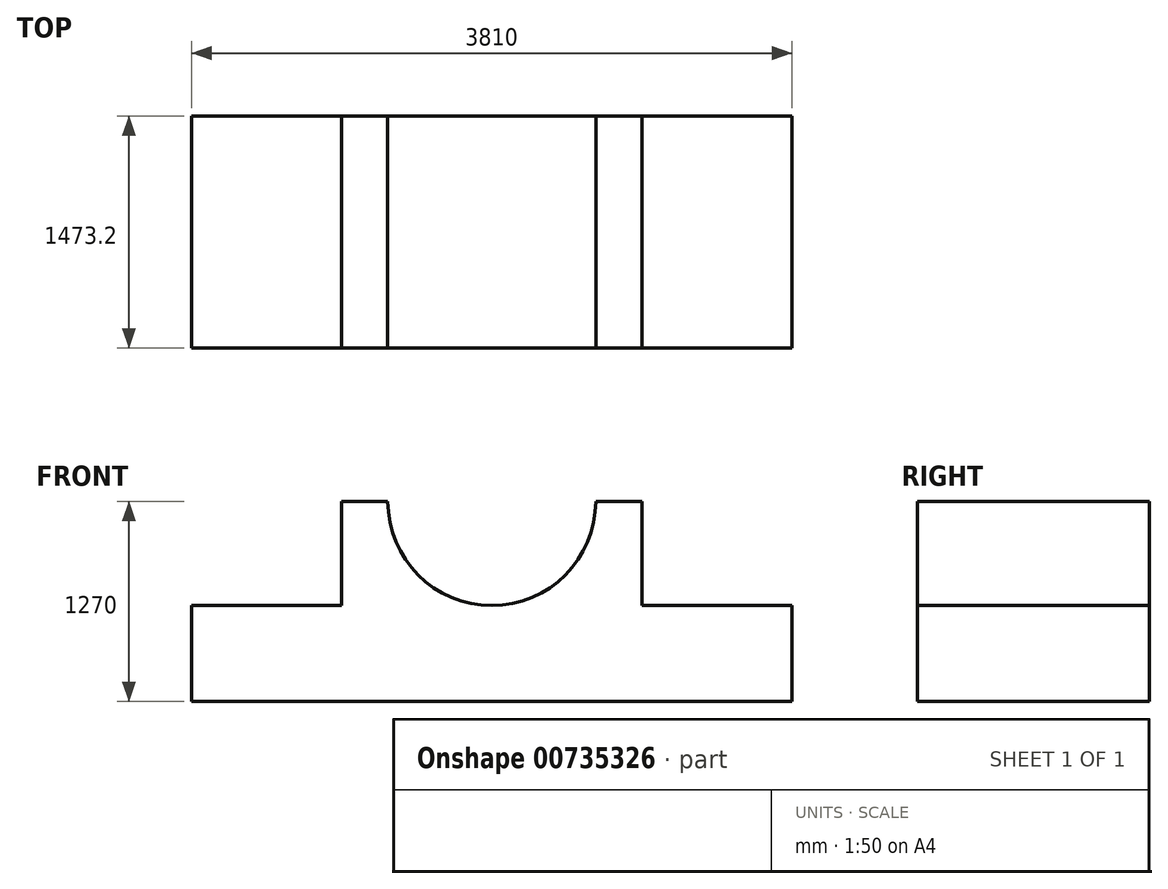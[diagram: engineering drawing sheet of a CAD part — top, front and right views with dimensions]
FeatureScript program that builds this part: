
annotation { "Feature Type Name" : "Feature", "Feature Type Description" : "" }
export const myFeature = defineFeature(function(context is Context, id is Id, definition is map)
    precondition{}
    {
        {
            var Q0;
            Q0=qCreatedBy(makeId("Front.planeOp"),FACE);
            var sketch = newSketch(context, id + "F0", { "sketchPlane" : qUnion([Q0])});
            skLineSegment(sketch, "E0", {"start": v(-110.83, -21.51) * mm, "end": v(3699.17, -21.51) * mm});
            skLineSegment(sketch, "E1", {"start": v(-110.83, -21.51) * mm, "end": v(-110.83, 588.09) * mm});
            skLineSegment(sketch, "E2", {"start": v(-110.83, 588.09) * mm, "end": v(841.67, 588.09) * mm});
            skLineSegment(sketch, "E3", {"start": v(841.67, 588.09) * mm, "end": v(841.67, 1248.49) * mm});
            skLineSegment(sketch, "E4", {"start": v(3699.17, -21.51) * mm, "end": v(3699.17, 588.09) * mm});
            skLineSegment(sketch, "E5", {"start": v(3699.17, 588.09) * mm, "end": v(2746.67, 588.09) * mm});
            skLineSegment(sketch, "E6", {"start": v(2746.67, 588.09) * mm, "end": v(2746.67, 1248.49) * mm});
            skLineSegment(sketch, "E7", {"start": v(2746.67, 1248.49) * mm, "end": v(841.67, 1248.49) * mm});
            skCircle(sketch, "E8", {"center": v(1794.17, 1248.49) * mm, "radius": 660.4 * mm});
            skSolve(sketch);
        }
        {
            var Q0;
            Q0=makeQuery(id+"F0.imprint","IMPRINT",FACE,{"disambiguationData":[TD([[makeQuery(id+"F0.imprint","IMPRINT",EDGE,{"derivedFrom":sQuery(id+"F0.wireOp",EDGE,"E0")}),1.0]])]});
            extrude(context, id + "F1", {"entities" : qUnion([Q0]), "depth" : 1473.2 * mm, "offsetDistance" : 25.4 * mm});
        }
    });
